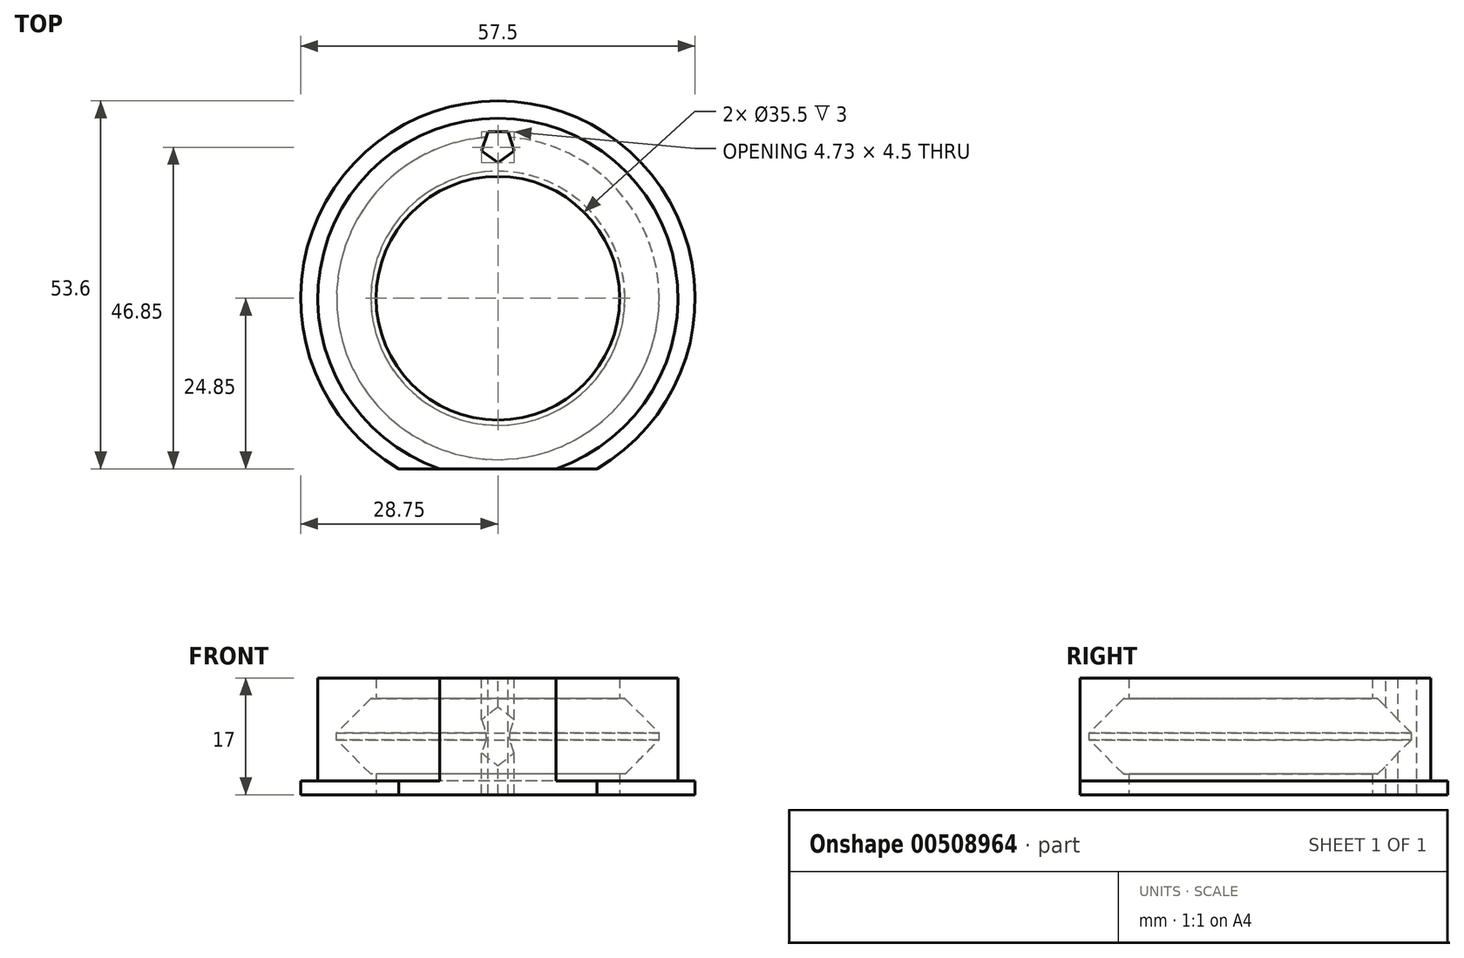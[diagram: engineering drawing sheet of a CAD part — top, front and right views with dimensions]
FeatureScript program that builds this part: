
annotation { "Feature Type Name" : "Feature", "Feature Type Description" : "" }
export const myFeature = defineFeature(function(context is Context, id is Id, definition is map)
    precondition{}
    {
        {
            var Q0;
            Q0=qCreatedBy(makeId("Top.planeOp"),FACE);
            var sketch = newSketch(context, id + "F0", { "sketchPlane" : qUnion([Q0])});
            skCircle(sketch, "E0", {"center": v(0, 0) * mm, "radius": 17.75 * mm});
            skCircle(sketch, "E1", {"center": v(0, 0) * mm, "radius": 26.25 * mm});
            skCircle(sketch, "E2", {"center": v(0, 0) * mm, "radius": 28.75 * mm});
            skSolve(sketch);
        }
        {
            var Q0;
            Q0=makeQuery(id+"F0.imprint","IMPRINT",FACE,{"disambiguationData":[TD([[makeQuery(id+"F0.imprint","IMPRINT",EDGE,{"derivedFrom":sQuery(id+"F0.wireOp",EDGE,"E0")}),-1.0]])]});
            extrude(context, id + "F1", {"entities" : qUnion([Q0]), "depth" : 17 * mm, "offsetDistance" : 25 * mm});
        }
        {
            var Q0;
            Q0=makeQuery(id+"F0.imprint","IMPRINT",FACE,{"disambiguationData":[TD([[makeQuery(id+"F0.imprint","IMPRINT",EDGE,{"derivedFrom":sQuery(id+"F0.wireOp",EDGE,"E1")}),-1.0]])]});
            extrude(context, id + "F2", {"entities" : qUnion([Q0]), "operationType" : NewBodyOperationType.ADD, "depth" : 2 * mm, "offsetDistance" : 25 * mm});
        }
        {
            var Q0;
            Q0=qCreatedBy(makeId("Top.planeOp"),FACE);
            cPlane(context, id + "F3", {"entities" : qUnion([Q0]), "cplaneType" : CPlaneType.OFFSET, "offset" : 8.5 * mm, "width" : 150 * mm, "height" : 150 * mm});
        }
        {
            var Q0;
            Q0=qCreatedBy(id+"F3.planeOp",FACE);
            var sketch = newSketch(context, id + "F4", { "sketchPlane" : qUnion([Q0])});
            skCircle(sketch, "E3", {"center": v(0, 0) * mm, "radius": 23.52 * mm});
            skSolve(sketch);
        }
        {
            var Q0;
            Q0 = qSketchRegion(id + "F4", true);
            extrude(context, id + "F5", {"entities" : qUnion([Q0]), "operationType" : NewBodyOperationType.REMOVE, "endBound" : BoundingType.SYMMETRIC, "oppositeDirection" : true, "depth" : 11 * mm, "offsetDistance" : 25 * mm});
        }
        {
            var Q0;
            Q0=makeQuery(id+"F5.boolean.opBoolean","COPY",EDGE,{"derivedFrom":makeQuery(id+"F5.opExtrude","CAP_EDGE",EDGE,{"disambiguationData":[OSD([sQuery(id+"F4.wireOp",EDGE,"E3")])],"isStart":false})});
            var Q1;
            Q1=makeQuery(id+"F5.boolean.opBoolean","COPY",EDGE,{"derivedFrom":makeQuery(id+"F5.opExtrude","CAP_EDGE",EDGE,{"disambiguationData":[OSD([sQuery(id+"F4.wireOp",EDGE,"E3")])],"isStart":true})});
            chamfer(context, id + "F6", {"entities" : qUnion([Q0, Q1]), "width" : 5 * mm, "tangentPropagation" : true});
        }
        {
            var Q0;
            Q0=makeQuery(id+"F1.opExtrude","CAP_FACE",FACE,{"disambiguationData":[OSD([sQuery(id+"F0.wireOp",EDGE,"E0"),sQuery(id+"F0.wireOp",EDGE,"E1")])],"isStart":false});
            var sketch = newSketch(context, id + "F7", { "sketchPlane" : qUnion([Q0])});
            skCircle(sketch, "E4.cCircle", {"center": v(0, 22.24) * mm, "radius": 2.01 * mm, "construction": true});
            skLineSegment(sketch, "E4.0", {"start": v(-1.46, 24.25) * mm, "end": v(1.46, 24.25) * mm});
            skLineSegment(sketch, "E4.1", {"start": v(1.46, 24.25) * mm, "end": v(2.37, 21.47) * mm});
            skLineSegment(sketch, "E4.2", {"start": v(2.37, 21.47) * mm, "end": v(0, 19.75) * mm});
            skLineSegment(sketch, "E4.3", {"start": v(0, 19.75) * mm, "end": v(-2.37, 21.47) * mm});
            skLineSegment(sketch, "E4.4", {"start": v(-2.37, 21.47) * mm, "end": v(-1.46, 24.25) * mm});
            skPoint(sketch, "E4.0.midPoint", {"position": v(0, 24.25) * mm});
            skLineSegment(sketch, "E5.bottom", {"start": v(-28.97, -24.85) * mm, "end": v(28.97, -24.85) * mm});
            skLineSegment(sketch, "E5.top", {"start": v(-28.97, -43.58) * mm, "end": v(28.97, -43.58) * mm});
            skLineSegment(sketch, "E5.left", {"start": v(-28.97, -24.85) * mm, "end": v(-28.97, -43.58) * mm});
            skLineSegment(sketch, "E5.right", {"start": v(28.97, -24.85) * mm, "end": v(28.97, -43.58) * mm});
            skPoint(sketch, "E5.middle", {"position": v(0, -34.22) * mm});
            skSolve(sketch);
        }
        {
            var Q0;
            Q0=makeQuery(id+"F7.imprint","IMPRINT",FACE,{"disambiguationData":[TD([[makeQuery(id+"F7.imprint","IMPRINT",EDGE,{"derivedFrom":sQuery(id+"F7.wireOp",EDGE,"E4.0")}),-1.0]])]});
            extrude(context, id + "F8", {"entities" : qUnion([Q0]), "operationType" : NewBodyOperationType.REMOVE, "oppositeDirection" : true, "depth" : 20 * mm, "offsetDistance" : 25 * mm});
        }
        {
            var Q0;
            Q0=makeQuery(id+"F7.imprint","IMPRINT",FACE,{"disambiguationData":[TD([[makeQuery(id+"F7.imprint","IMPRINT",EDGE,{"derivedFrom":sQuery(id+"F7.wireOp",EDGE,"E5.top")}),1.0]])]});
            var Q1;
            {var subQ0=sQuery(id+"F7.wireOp",EDGE,"E5.bottom");var subQ1=makeQuery(id+"F1.opExtrude","CAP_EDGE",EDGE,{"disambiguationData":[OSD([sQuery(id+"F0.wireOp",EDGE,"E1")])],"isStart":false});var subQ2=makeQuery(id+"F7.imprint","INTERSECT",VERTEX,{"disambiguationData":[OD(0.0)],"derivedFrom":[subQ1,subQ0]});Q1=makeQuery(id+"F7.imprint","IMPRINT",FACE,{"disambiguationData":[TD([[makeQuery(id+"F7.imprint","IMPRINT",EDGE,{"disambiguationData":[TD([[subQ2,-1.0]])],"derivedFrom":subQ0}),-1.0]])]});}
            extrude(context, id + "F9", {"entities" : qUnion([Q0, Q1]), "operationType" : NewBodyOperationType.REMOVE, "oppositeDirection" : true, "depth" : 29.9 * mm, "offsetDistance" : 25 * mm});
        }
    });
